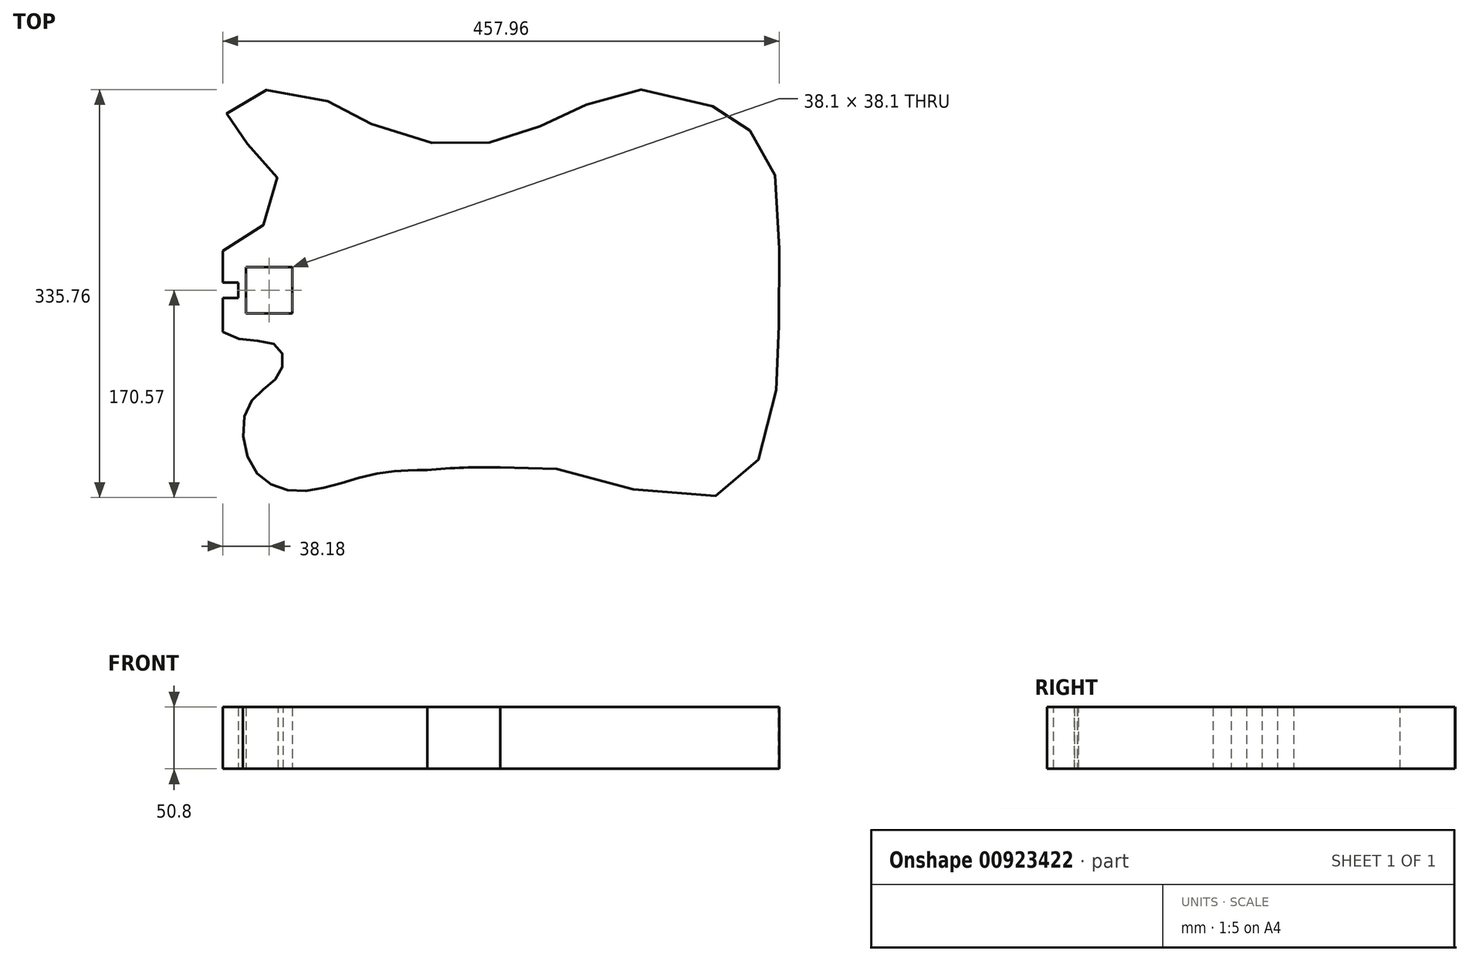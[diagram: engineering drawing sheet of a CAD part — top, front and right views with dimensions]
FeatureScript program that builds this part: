
annotation { "Feature Type Name" : "Feature", "Feature Type Description" : "" }
export const myFeature = defineFeature(function(context is Context, id is Id, definition is map)
    precondition{}
    {
        {
            var Q0;
            Q0=qCreatedBy(makeId("Top.planeOp"),FACE);
            var sketch = newSketch(context, id + "F0", { "sketchPlane" : qUnion([Q0])});
            skLineSegment(sketch, "E0.bottom", {"start": v(-189.97, 165.1) * mm, "end": v(-183.45, 165.1) * mm, "construction": true});
            skLineSegment(sketch, "E0.top", {"start": v(-169.47, -165.1) * mm, "end": v(-160.67, -165.1) * mm, "construction": true});
            skLineSegment(sketch, "E0.right", {"start": v(228.6, 0) * mm, "end": v(228.6, -13.35) * mm, "construction": true});
            skPoint(sketch, "E0.middle", {"position": v(0, 0) * mm});
            skPoint(sketch, "E1.endSnap0", {"position": v(0, 165.1) * mm});
            skLineSegment(sketch, "E2", {"start": v(-228.6, 6.35) * mm, "end": v(-228.6, -6.35) * mm});
            skLineSegment(sketch, "E3", {"start": v(-228.6, -6.35) * mm, "end": v(-215.9, -6.35) * mm});
            skLineSegment(sketch, "E4", {"start": v(-215.9, -6.35) * mm, "end": v(-215.9, 6.35) * mm});
            skLineSegment(sketch, "E5", {"start": v(-215.9, 6.35) * mm, "end": v(-228.6, 6.35) * mm});
            skPoint(sketch, "E6", {"position": v(-228.6, 0) * mm});
            skLineSegment(sketch, "E7", {"start": v(-209.55, 19.05) * mm, "end": v(-209.55, -19.05) * mm});
            skLineSegment(sketch, "E8", {"start": v(-209.55, 19.05) * mm, "end": v(-171.45, 19.05) * mm});
            skLineSegment(sketch, "E9", {"start": v(-171.45, -19.05) * mm, "end": v(-171.45, 19.05) * mm});
            skLineSegment(sketch, "E10", {"start": v(-171.45, -19.05) * mm, "end": v(-209.55, -19.05) * mm});
            skPoint(sketch, "E11", {"position": v(-209.55, 0) * mm});
            skLineSegment(sketch, "E12", {"start": v(-228.6, 0) * mm, "end": v(228.6, 0) * mm, "construction": true});
            skPoint(sketch, "E13.26.internal.snap0", {"position": v(0, -165.1) * mm});
            skFitSpline(sketch, "E14", {"points": [v(-228.6, 32.2) * mm, v(-203.44, 48.03) * mm, v(-184.24, 71.25) * mm, v(-188.25, 103.93) * mm, v(-208.03, 119.98) * mm, v(-228.6, 136.9) * mm, v(-215.77, 154.39) * mm, v(-189.97, 165.1) * mm, v(-140.37, 154.67) * mm, v(-116, 141.49) * mm, v(-69.85, 124) * mm, v(-25.41, 119.98) * mm, v(13, 126.86) * mm, v(44.25, 140.63) * mm, v(74.64, 154.67) * mm, v(116.21, 165.1) * mm, v(179.9, 148.85) * mm, v(199.09, 136.72) * mm, v(218.55, 114.44) * mm, v(228.6, 70.15) * mm, v(228.6, -13.35) * mm, v(228.6, -65.16) * mm, v(215.19, -130.68) * mm, v(190.73, -165.1) * mm, v(115.15, -165.1) * mm, v(39.56, -145.87) * mm, v(0, -145.87) * mm, v(-60.5, -148.16) * mm, v(-73.93, -148.16) * mm, v(-110.95, -152.88) * mm, v(-160.67, -165.1) * mm, v(-202.05, -148.89) * mm, v(-207.5, -94.8) * mm, v(-181.72, -68.32) * mm, v(-184.99, -45.09) * mm, v(-228.6, -34.2) * mm, v(-228.6, 32.2) * mm]});
            skLineSegment(sketch, "E15.trimOffspring", {"start": v(-228.6, 6.35) * mm, "end": v(-228.6, -34.2) * mm, "construction": true});
            skPoint(sketch, "E16.start.orphan", {"position": v(-228.6, 19.27) * mm});
            skPoint(sketch, "E17.orphan", {"position": v(-228.6, 12.81) * mm});
            skLineSegment(sketch, "E18", {"start": v(-228.6, 32.2) * mm, "end": v(-228.6, 6.35) * mm});
            skLineSegment(sketch, "E19", {"start": v(-228.6, -34.2) * mm, "end": v(-228.6, -6.35) * mm});
            skArc(sketch, "E20", {"start": v(-0.28, -145.89) * mm, "mid": v(-30.43, -146.01) * mm, "end": v(-60.5, -148.16) * mm});
            skLineSegment(sketch, "E21.trimOffspring", {"start": v(113.81, 165.1) * mm, "end": v(116.21, 165.1) * mm, "construction": true});
            skPoint(sketch, "E22.orphan", {"position": v(-228.6, 165.1) * mm});
            skPoint(sketch, "E23.orphan", {"position": v(228.6, 165.1) * mm});
            skLineSegment(sketch, "E24.trimOffspring", {"start": v(190.73, -165.1) * mm, "end": v(228.6, -165.1) * mm, "construction": true});
            skPoint(sketch, "E25.orphan", {"position": v(-228.6, -165.1) * mm});
            skSolve(sketch);
        }
        {
            var Q0;
            Q0=makeQuery(id+"F0.imprint","IMPRINT",FACE,{"disambiguationData":[TD([[makeQuery(id+"F0.imprint","IMPRINT",EDGE,{"derivedFrom":sQuery(id+"F0.wireOp",EDGE,"E3")}),-1.0]])]});
            extrude(context, id + "F1", {"entities" : qUnion([Q0]), "depth" : 50.8 * mm, "offsetDistance" : 25.4 * mm});
        }
    });
